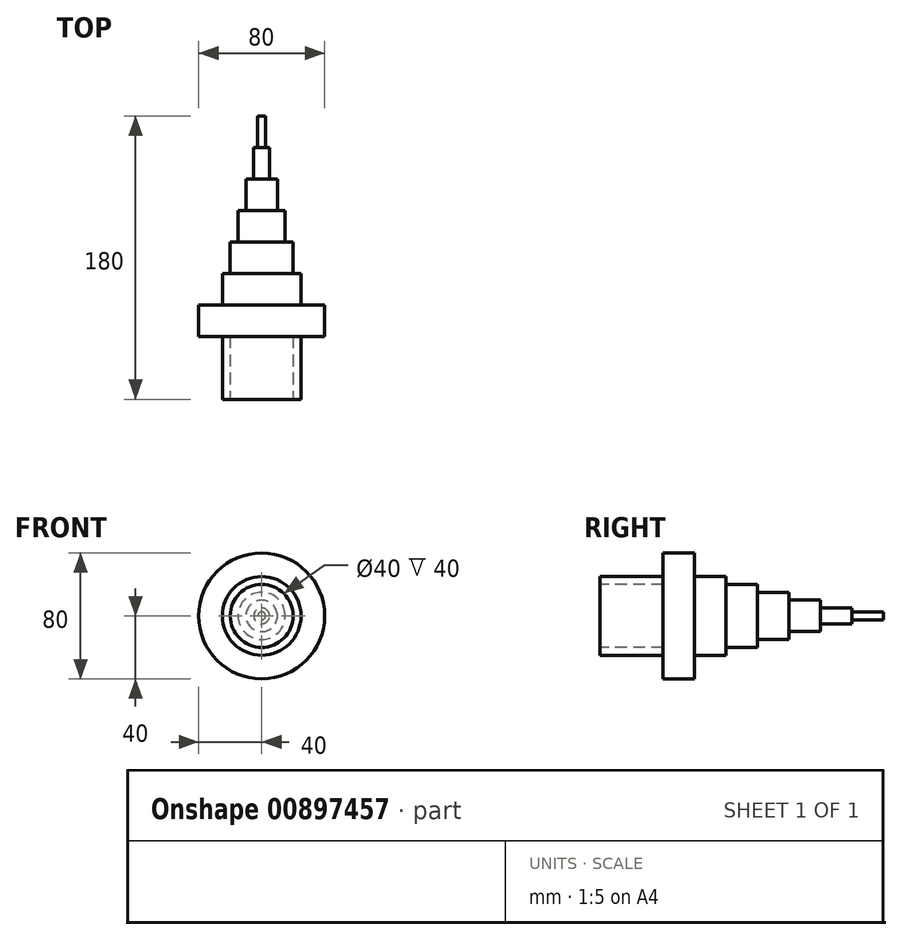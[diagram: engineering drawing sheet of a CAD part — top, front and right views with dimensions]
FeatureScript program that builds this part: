
annotation { "Feature Type Name" : "Feature", "Feature Type Description" : "" }
export const myFeature = defineFeature(function(context is Context, id is Id, definition is map)
    precondition{}
    {
        {
            var Q0;
            Q0=qCreatedBy(makeId("Front.planeOp"),FACE);
            var sketch = newSketch(context, id + "F0", { "sketchPlane" : qUnion([Q0])});
            skCircle(sketch, "E0", {"center": v(0, 0) * mm, "radius": 40 * mm});
            skSolve(sketch);
        }
        {
            var Q0;
            Q0=makeQuery(id+"F0.imprint","IMPRINT",FACE,{"disambiguationData":[TD([[makeQuery(id+"F0.imprint","IMPRINT",EDGE,{"derivedFrom":sQuery(id+"F0.wireOp",EDGE,"E0")}),1.0]])]});
            extrude(context, id + "F1", {"entities" : qUnion([Q0]), "depth" : 20 * mm, "offsetDistance" : 25.4 * mm});
        }
        {
            var Q0;
            Q0=makeQuery(id+"F1.opExtrude","CAP_FACE",FACE,{"disambiguationData":[OSD([sQuery(id+"F0.wireOp",EDGE,"E0")])],"isStart":false});
            var sketch = newSketch(context, id + "F2", { "sketchPlane" : qUnion([Q0])});
            skCircle(sketch, "E1", {"center": v(0, 0) * mm, "radius": 25 * mm});
            skSolve(sketch);
        }
        {
            var Q0;
            Q0=makeQuery(id+"F2.imprint","IMPRINT",FACE,{"disambiguationData":[TD([[makeQuery(id+"F2.imprint","IMPRINT",EDGE,{"derivedFrom":sQuery(id+"F2.wireOp",EDGE,"E1")}),1.0]])]});
            extrude(context, id + "F3", {"entities" : qUnion([Q0]), "operationType" : NewBodyOperationType.ADD, "depth" : 40 * mm, "offsetDistance" : 25.4 * mm});
        }
        {
            var Q0;
            Q0=makeQuery(id+"F3.opExtrude","CAP_FACE",FACE,{"disambiguationData":[OSD([sQuery(id+"F2.wireOp",EDGE,"E1")])],"isStart":false});
            var sketch = newSketch(context, id + "F4", { "sketchPlane" : qUnion([Q0])});
            skCircle(sketch, "E2", {"center": v(0, 0) * mm, "radius": 20 * mm});
            skSolve(sketch);
        }
        {
            var Q0;
            Q0=makeQuery(id+"F4.imprint","IMPRINT",FACE,{"disambiguationData":[TD([[makeQuery(id+"F4.imprint","IMPRINT",EDGE,{"derivedFrom":sQuery(id+"F4.wireOp",EDGE,"E2")}),1.0]])]});
            extrude(context, id + "F5", {"entities" : qUnion([Q0]), "operationType" : NewBodyOperationType.REMOVE, "oppositeDirection" : true, "depth" : 40 * mm, "offsetDistance" : 25.4 * mm});
        }
        {
            var Q0;
            Q0=makeQuery(id+"F1.opExtrude","CAP_FACE",FACE,{"disambiguationData":[OSD([sQuery(id+"F0.wireOp",EDGE,"E0")])],"isStart":true});
            var sketch = newSketch(context, id + "F6", { "sketchPlane" : qUnion([Q0])});
            skCircle(sketch, "E3", {"center": v(0, 0) * mm, "radius": 25 * mm});
            skSolve(sketch);
        }
        {
            var Q0;
            Q0=makeQuery(id+"F6.imprint","IMPRINT",FACE,{"disambiguationData":[TD([[makeQuery(id+"F6.imprint","IMPRINT",EDGE,{"derivedFrom":sQuery(id+"F6.wireOp",EDGE,"E3")}),1.0]])]});
            extrude(context, id + "F7", {"entities" : qUnion([Q0]), "operationType" : NewBodyOperationType.ADD, "depth" : 20 * mm, "offsetDistance" : 25.4 * mm});
        }
        {
            var Q0;
            Q0=makeQuery(id+"F7.opExtrude","CAP_FACE",FACE,{"disambiguationData":[OSD([sQuery(id+"F6.wireOp",EDGE,"E3")])],"isStart":false});
            var sketch = newSketch(context, id + "F8", { "sketchPlane" : qUnion([Q0])});
            skCircle(sketch, "E4", {"center": v(0, 0) * mm, "radius": 20 * mm});
            skSolve(sketch);
        }
        {
            var Q0;
            Q0=makeQuery(id+"F8.imprint","IMPRINT",FACE,{"disambiguationData":[TD([[makeQuery(id+"F8.imprint","IMPRINT",EDGE,{"derivedFrom":sQuery(id+"F8.wireOp",EDGE,"E4")}),1.0]])]});
            extrude(context, id + "F9", {"entities" : qUnion([Q0]), "operationType" : NewBodyOperationType.ADD, "depth" : 20 * mm, "offsetDistance" : 25.4 * mm});
        }
        {
            var Q0;
            Q0=makeQuery(id+"F9.opExtrude","CAP_FACE",FACE,{"disambiguationData":[OSD([sQuery(id+"F8.wireOp",EDGE,"E4")])],"isStart":false});
            var sketch = newSketch(context, id + "F10", { "sketchPlane" : qUnion([Q0])});
            skCircle(sketch, "E5", {"center": v(0, 0) * mm, "radius": 15 * mm});
            skSolve(sketch);
        }
        {
            var Q0;
            Q0=makeQuery(id+"F10.imprint","IMPRINT",FACE,{"disambiguationData":[TD([[makeQuery(id+"F10.imprint","IMPRINT",EDGE,{"derivedFrom":sQuery(id+"F10.wireOp",EDGE,"E5")}),1.0]])]});
            extrude(context, id + "F11", {"entities" : qUnion([Q0]), "operationType" : NewBodyOperationType.ADD, "depth" : 20 * mm, "offsetDistance" : 25.4 * mm});
        }
        {
            var Q0;
            Q0=makeQuery(id+"F11.opExtrude","CAP_FACE",FACE,{"disambiguationData":[OSD([sQuery(id+"F10.wireOp",EDGE,"E5")])],"isStart":false});
            var sketch = newSketch(context, id + "F12", { "sketchPlane" : qUnion([Q0])});
            skCircle(sketch, "E6", {"center": v(0, 0) * mm, "radius": 10 * mm});
            skSolve(sketch);
        }
        {
            var Q0;
            Q0=makeQuery(id+"F12.imprint","IMPRINT",FACE,{"disambiguationData":[TD([[makeQuery(id+"F12.imprint","IMPRINT",EDGE,{"derivedFrom":sQuery(id+"F12.wireOp",EDGE,"E6")}),1.0]])]});
            extrude(context, id + "F13", {"entities" : qUnion([Q0]), "operationType" : NewBodyOperationType.ADD, "depth" : 20 * mm, "offsetDistance" : 25.4 * mm});
        }
        {
            var Q0;
            Q0=makeQuery(id+"F13.opExtrude","CAP_FACE",FACE,{"disambiguationData":[OSD([sQuery(id+"F12.wireOp",EDGE,"E6")])],"isStart":false});
            var sketch = newSketch(context, id + "F14", { "sketchPlane" : qUnion([Q0])});
            skCircle(sketch, "E7", {"center": v(0, 0) * mm, "radius": 5 * mm});
            skSolve(sketch);
        }
        {
            var Q0;
            Q0=makeQuery(id+"F14.imprint","IMPRINT",FACE,{"disambiguationData":[TD([[makeQuery(id+"F14.imprint","IMPRINT",EDGE,{"derivedFrom":sQuery(id+"F14.wireOp",EDGE,"E7")}),1.0]])]});
            extrude(context, id + "F15", {"entities" : qUnion([Q0]), "operationType" : NewBodyOperationType.ADD, "depth" : 20 * mm, "offsetDistance" : 25.4 * mm});
        }
        {
            var Q0;
            Q0=makeQuery(id+"F15.opExtrude","CAP_FACE",FACE,{"disambiguationData":[OSD([sQuery(id+"F14.wireOp",EDGE,"E7")])],"isStart":false});
            var sketch = newSketch(context, id + "F16", { "sketchPlane" : qUnion([Q0])});
            skCircle(sketch, "E8", {"center": v(0, 0) * mm, "radius": 2.5 * mm});
            skSolve(sketch);
        }
        {
            var Q0;
            Q0=makeQuery(id+"F16.imprint","IMPRINT",FACE,{"disambiguationData":[TD([[makeQuery(id+"F16.imprint","IMPRINT",EDGE,{"derivedFrom":sQuery(id+"F16.wireOp",EDGE,"E8")}),1.0]])]});
            extrude(context, id + "F17", {"entities" : qUnion([Q0]), "operationType" : NewBodyOperationType.ADD, "depth" : 20 * mm, "offsetDistance" : 25.4 * mm});
        }
    });
